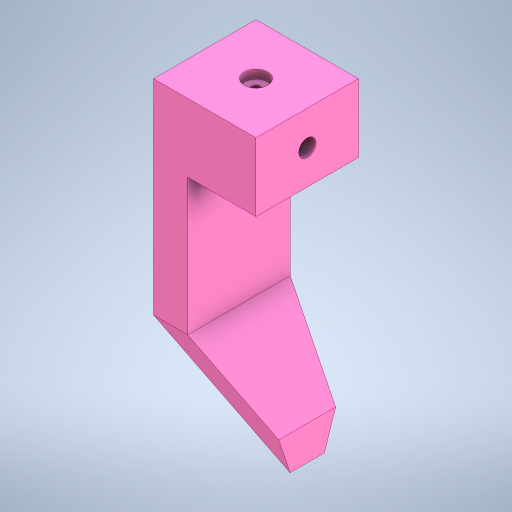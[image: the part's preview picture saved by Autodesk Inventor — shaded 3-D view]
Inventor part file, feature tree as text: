
AUTODESK INVENTOR PART (.ipt)
format: ipt  version: 2024 (Build 280153000, 153)  size: 279,552 bytes
history: native  units: in
note: dims shown in document units (in); Inventor stores cm internally (conversion verified against a paired STEP export)
features: extrude x5, sketch x5, plane x1
ambient origin geometry x8: Origin, YZ Plane, XZ Plane, XY Plane, X Axis, Y Axis, Z Axis, Center Point
bodies: Solid1 (feature_tree)
feature tree (11):
  extrude  "Extrusion1"  Depth=2.0in
  plane  "Work Plane1"
  extrude  "Extrusion2"  Depth=1.0in
  extrude  "Extrusion3"  Depth=3.0in TaperAngle=0.0deg
  extrude  "Extrusion4"  Depth=0.7071in
  extrude  "Extrusion5"  Depth=0.125in
  sketch  "Sketch1"  dims[d11=4.0in d12=2.0in]
  sketch  "Sketch2"  dims[d13=1.0in d17=1.1231in]
  sketch  "Sketch3"  dims[d18=2.0in d20=3.0in d21=0.0in]
  sketch  "Sketch4"  dims[d23=135.0deg d24=0.7071in]
  sketch  "Sketch5"  dims[d25=2.0in d26=6.0in d27=2.0in d28=1.0in d29=1.0in d30=7.0in d31=0.0in d32=1.5in d33=1.5in d34=0.688in d35=0.25in d36=0.0in d39=0.5in d40=1.5in d41=1.0in d42=6.0625in d43=0.0in d44=0.25in d45=0.125in d46=0.0in]
